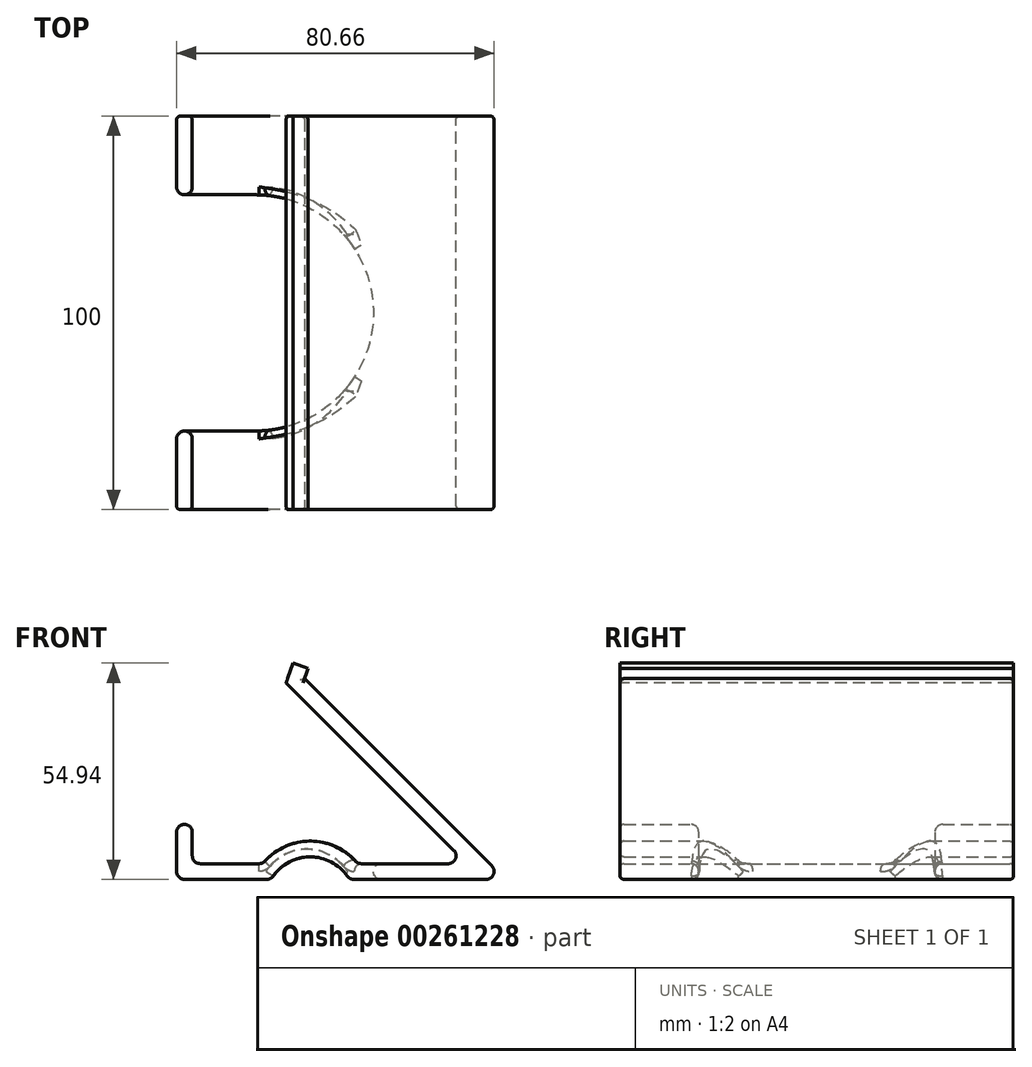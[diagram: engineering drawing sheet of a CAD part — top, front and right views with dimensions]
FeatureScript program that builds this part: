
annotation { "Feature Type Name" : "Feature", "Feature Type Description" : "" }
export const myFeature = defineFeature(function(context is Context, id is Id, definition is map)
    precondition{}
    {
        {
            var Q0;
            Q0=qCreatedBy(makeId("Front.planeOp"),FACE);
            var sketch = newSketch(context, id + "F0", { "sketchPlane" : qUnion([Q0])});
            skLineSegment(sketch, "E0", {"start": v(-39.92, 0) * mm, "end": v(-19.92, 0) * mm});
            skLineSegment(sketch, "E1", {"start": v(-39.92, 4) * mm, "end": v(-39.92, 10) * mm});
            skLineSegment(sketch, "E2", {"start": v(0, 0) * mm, "end": v(0.08, 0) * mm});
            skArc(sketch, "E3", {"start": v(0, 0) * mm, "mid": v(-9.96, 5.74) * mm, "end": v(-19.92, 0) * mm});
            skLineSegment(sketch, "E4.trimOffspring", {"start": v(0, 0) * mm, "end": v(39.57, 0) * mm});
            skLineSegment(sketch, "E5", {"start": v(-0.18, 39.75) * mm, "end": v(39.57, 0) * mm});
            skLineSegment(sketch, "E6.0", {"start": v(2.09, 4) * mm, "end": v(29.91, 4) * mm});
            skLineSegment(sketch, "E6.1", {"start": v(-3, 36.92) * mm, "end": v(29.91, 4) * mm});
            skArc(sketch, "E7.0", {"start": v(2.09, 4) * mm, "mid": v(-9.96, 9.74) * mm, "end": v(-22.01, 4) * mm});
            skLineSegment(sketch, "E8.0", {"start": v(-39.92, 4) * mm, "end": v(-22.01, 4) * mm});
            skLineSegment(sketch, "E9.0", {"start": v(-43.92, 0) * mm, "end": v(-43.92, 10) * mm});
            skLineSegment(sketch, "E10", {"start": v(-39.92, 4) * mm, "end": v(-39.92, 14) * mm});
            skLineSegment(sketch, "E11", {"start": v(-39.92, 14) * mm, "end": v(-43.92, 14) * mm});
            skLineSegment(sketch, "E12", {"start": v(-43.92, 14) * mm, "end": v(-43.92, 10) * mm});
            skLineSegment(sketch, "E13", {"start": v(-43.92, 0) * mm, "end": v(-39.92, 0) * mm});
            skLineSegment(sketch, "E14", {"start": v(-0.18, 39.75) * mm, "end": v(-3, 36.92) * mm});
            skSolve(sketch);
        }
        {
            var Q0;
            Q0 = qSketchRegion(id + "F0", true);
            extrude(context, id + "F1", {"entities" : qUnion([Q0]), "depth" : 100 * mm});
        }
        {
            var Q0;
            Q0=makeQuery(id+"F1.opExtrude","SWEPT_FACE",FACE,{"disambiguationData":[OSD([sQuery(id+"F0.wireOp",EDGE,"E14")])]});
            extrude(context, id + "F2", {"entities" : qUnion([Q0]), "operationType" : NewBodyOperationType.ADD, "depth" : 19.5 * mm});
        }
        {
            var Q0;
            {var subQ0=sQuery(id+"F0.wireOp",EDGE,"E14");Q0=makeQuery(id+"F2.boolean.opBoolean","MERGE",FACE,{"derivedFrom":[makeQuery(id+"F1.opExtrude","CAP_FACE",FACE,{"disambiguationData":[OSD([sQuery(id+"F0.wireOp",EDGE,"E0"),sQuery(id+"F0.wireOp",EDGE,"E3"),sQuery(id+"F0.wireOp",EDGE,"E4.trimOffspring"),sQuery(id+"F0.wireOp",EDGE,"E5"),sQuery(id+"F0.wireOp",EDGE,"E6.0"),sQuery(id+"F0.wireOp",EDGE,"E6.1"),sQuery(id+"F0.wireOp",EDGE,"E7.0"),sQuery(id+"F0.wireOp",EDGE,"E8.0"),sQuery(id+"F0.wireOp",EDGE,"E9.0"),sQuery(id+"F0.wireOp",EDGE,"E10"),sQuery(id+"F0.wireOp",EDGE,"E11"),sQuery(id+"F0.wireOp",EDGE,"E12"),sQuery(id+"F0.wireOp",EDGE,"E13"),subQ0])],"isStart":false}),makeQuery(id+"F2.opExtrude","SWEPT_FACE",FACE,{"disambiguationData":[OSD([subQ0]),TDD([makeQuery(id+"F1.opExtrude","CAP_EDGE",EDGE,{"disambiguationData":[OSD([subQ0])],"isStart":false})])]})]});}
            var sketch = newSketch(context, id + "F3", { "sketchPlane" : qUnion([Q0])});
            skLineSegment(sketch, "E15.0.1", {"start": v(-39.92, 4) * mm, "end": v(-39.92, 14) * mm});
            skLineSegment(sketch, "E15.0.2", {"start": v(-39.92, 14) * mm, "end": v(-43.92, 14) * mm});
            skLineSegment(sketch, "E15.0.3", {"start": v(-43.92, 14) * mm, "end": v(-43.92, 0) * mm});
            skArc(sketch, "E15.0.5", {"start": v(-19.92, 0) * mm, "mid": v(-9.96, 5.74) * mm, "end": v(0, 0) * mm});
            skLineSegment(sketch, "E15.0.6", {"start": v(0, 0) * mm, "end": v(39.57, 0) * mm});
            skArc(sketch, "E15.0.11", {"start": v(2.09, 4) * mm, "mid": v(-9.96, 9.74) * mm, "end": v(-22.01, 4) * mm});
            skLineSegment(sketch, "E16.0", {"start": v(-13.97, 53.54) * mm, "end": v(-16.8, 50.7) * mm});
            skLineSegment(sketch, "E17.0", {"start": v(-13.97, 53.54) * mm, "end": v(-12.16, 51.73) * mm});
            skLineSegment(sketch, "E18", {"start": v(-15.24, 52.26) * mm, "end": v(19.9, 148.83) * mm});
            skLineSegment(sketch, "E19.0", {"start": v(-11.44, 51.01) * mm, "end": v(23.66, 147.46) * mm});
            skLineSegment(sketch, "E20.0", {"start": v(-13.97, 53.54) * mm, "end": v(39.57, 0) * mm});
            skLineSegment(sketch, "E21", {"start": v(19.9, 148.83) * mm, "end": v(23.66, 147.46) * mm});
            skSolve(sketch);
        }
        {
            var Q0;
            Q0 = qSketchRegion(id + "F3", true);
            extrude(context, id + "F4", {"entities" : qUnion([Q0]), "operationType" : NewBodyOperationType.ADD, "oppositeDirection" : true, "depth" : 100 * mm});
        }
        {
            var Q0;
            {var subQ0=sQuery(id+"F0.wireOp",EDGE,"E14");Q0=makeQuery(id+"F4.boolean.opBoolean","MERGE",FACE,{"derivedFrom":[makeQuery(id+"F2.boolean.opBoolean","MERGE",FACE,{"derivedFrom":[makeQuery(id+"F1.opExtrude","CAP_FACE",FACE,{"disambiguationData":[OSD([sQuery(id+"F0.wireOp",EDGE,"E0"),sQuery(id+"F0.wireOp",EDGE,"E3"),sQuery(id+"F0.wireOp",EDGE,"E4.trimOffspring"),sQuery(id+"F0.wireOp",EDGE,"E5"),sQuery(id+"F0.wireOp",EDGE,"E6.0"),sQuery(id+"F0.wireOp",EDGE,"E6.1"),sQuery(id+"F0.wireOp",EDGE,"E7.0"),sQuery(id+"F0.wireOp",EDGE,"E8.0"),sQuery(id+"F0.wireOp",EDGE,"E9.0"),sQuery(id+"F0.wireOp",EDGE,"E10"),sQuery(id+"F0.wireOp",EDGE,"E11"),sQuery(id+"F0.wireOp",EDGE,"E12"),sQuery(id+"F0.wireOp",EDGE,"E13"),subQ0])],"isStart":false}),makeQuery(id+"F2.opExtrude","SWEPT_FACE",FACE,{"disambiguationData":[OSD([subQ0]),TDD([makeQuery(id+"F1.opExtrude","CAP_EDGE",EDGE,{"disambiguationData":[OSD([subQ0])],"isStart":false})])]})]}),makeQuery(id+"F4.opExtrude","CAP_FACE",FACE,{"disambiguationData":[OSD([sQuery(id+"F3.wireOp",EDGE,"E16.0"),sQuery(id+"F3.wireOp",EDGE,"E18"),sQuery(id+"F3.wireOp",EDGE,"E19.0"),sQuery(id+"F3.wireOp",EDGE,"E20.0"),sQuery(id+"F3.wireOp",EDGE,"E21")])],"isStart":true})]});}
            var sketch = newSketch(context, id + "F5", { "sketchPlane" : qUnion([Q0])});
            skLineSegment(sketch, "E22.0", {"start": v(-16.8, 50.7) * mm, "end": v(-16.07, 49.98) * mm});
            skLineSegment(sketch, "E23", {"start": v(-15.24, 52.26) * mm, "end": v(-16.07, 49.98) * mm});
            skLineSegment(sketch, "E24", {"start": v(-15.24, 52.26) * mm, "end": v(-16.8, 50.7) * mm});
            skPoint(sketch, "E25.orphan", {"position": v(29.91, 4) * mm});
            skPoint(sketch, "E26.0.end.orphan", {"position": v(19.9, 148.83) * mm});
            skSolve(sketch);
        }
        {
            var Q0;
            Q0=makeQuery(id+"F5.imprint","IMPRINT",FACE,{"disambiguationData":[TD([[makeQuery(id+"F5.imprint","IMPRINT",EDGE,{"derivedFrom":sQuery(id+"F5.wireOp",EDGE,"E22.0")}),1.0]])]});
            extrude(context, id + "F6", {"entities" : qUnion([Q0]), "operationType" : NewBodyOperationType.REMOVE, "oppositeDirection" : true, "depth" : 108.1 * mm});
        }
        {
            var Q0;
            Q0=makeQuery(id+"F1.opExtrude","SWEPT_EDGE",EDGE,{"disambiguationData":[OSD([sQuery(id+"F0.wireOp",EDGE,"E8.0"),sQuery(id+"F0.wireOp",EDGE,"E10")])]});
            var Q1;
            Q1=makeQuery(id+"F6.boolean.opBoolean","COPY",EDGE,{"derivedFrom":makeQuery(id+"F6.opExtrude","SWEPT_EDGE",EDGE,{"disambiguationData":[OSD([sQuery(id+"F0.wireOp",EDGE,"E6.1"),sQuery(id+"F0.wireOp",EDGE,"E14"),sQuery(id+"F5.wireOp",EDGE,"E22.0"),sQuery(id+"F5.wireOp",EDGE,"E23")])]})});
            var Q2;
            Q2=makeQuery(id+"F4.opExtrude","SWEPT_EDGE",EDGE,{"disambiguationData":[OSD([sQuery(id+"F3.wireOp",EDGE,"E19.0"),sQuery(id+"F3.wireOp",EDGE,"E20.0")])]});
            var Q3;
            Q3=makeQuery(id+"F1.opExtrude","SWEPT_EDGE",EDGE,{"disambiguationData":[OSD([sQuery(id+"F0.wireOp",EDGE,"E4.trimOffspring"),sQuery(id+"F0.wireOp",EDGE,"E5")])]});
            var Q4;
            Q4=makeQuery(id+"F1.opExtrude","SWEPT_EDGE",EDGE,{"disambiguationData":[OSD([sQuery(id+"F0.wireOp",EDGE,"E6.0"),sQuery(id+"F0.wireOp",EDGE,"E6.1")])]});
            var Q5;
            Q5=makeQuery(id+"F1.opExtrude","SWEPT_EDGE",EDGE,{"disambiguationData":[OSD([sQuery(id+"F0.wireOp",EDGE,"E9.0"),sQuery(id+"F0.wireOp",EDGE,"E13")])]});
            var Q6;
            Q6=makeQuery(id+"F1.opExtrude","SWEPT_EDGE",EDGE,{"disambiguationData":[OSD([sQuery(id+"F0.wireOp",EDGE,"E0"),sQuery(id+"F0.wireOp",EDGE,"E3")])]});
            var Q7;
            Q7=makeQuery(id+"F1.opExtrude","SWEPT_EDGE",EDGE,{"disambiguationData":[OSD([sQuery(id+"F0.wireOp",EDGE,"E3"),sQuery(id+"F0.wireOp",EDGE,"E4.trimOffspring")])]});
            var Q8;
            Q8=makeQuery(id+"F1.opExtrude","SWEPT_EDGE",EDGE,{"disambiguationData":[OSD([sQuery(id+"F0.wireOp",EDGE,"E7.0"),sQuery(id+"F0.wireOp",EDGE,"E8.0")])]});
            var Q9;
            Q9=makeQuery(id+"F1.opExtrude","SWEPT_EDGE",EDGE,{"disambiguationData":[OSD([sQuery(id+"F0.wireOp",EDGE,"E6.0"),sQuery(id+"F0.wireOp",EDGE,"E7.0")])]});
            var Q10;
            Q10=makeQuery(id+"F1.opExtrude","SWEPT_EDGE",EDGE,{"disambiguationData":[OSD([sQuery(id+"F0.wireOp",EDGE,"E11"),sQuery(id+"F0.wireOp",EDGE,"E12")])]});
            fillet(context, id + "F7", {"entities" : qUnion([Q0, Q1, Q2, Q3, Q4, Q5, Q6, Q7, Q8, Q9, Q10]), "radius" : 2 * mm, "tangentPropagation" : true, "allowEdgeOverflow" : false});
        }
        {
            var Q0;
            {var subQ0=sQuery(id+"F0.wireOp",EDGE,"E14");var subQ1=sQuery(id+"F0.wireOp",EDGE,"E6.1");Q0=makeQuery(id+"F2.boolean.opBoolean","MERGE",EDGE,{"derivedFrom":[makeQuery(id+"F1.opExtrude","CAP_EDGE",EDGE,{"disambiguationData":[OSD([subQ1])],"isStart":true}),makeQuery(id+"F2.opExtrude","SWEPT_EDGE",EDGE,{"disambiguationData":[OSD([subQ1,subQ0]),TDD([makeQuery(id+"F1.opExtrude","CAP_VERTEX",VERTEX,{"disambiguationData":[OSD([subQ1,subQ0])],"isStart":true})])]})]});}
            var Q1;
            Q1=makeQuery(id+"F6.boolean.opBoolean","MERGE",EDGE,{"derivedFrom":[makeQuery(id+"F4.opExtrude","CAP_EDGE",EDGE,{"disambiguationData":[OSD([sQuery(id+"F3.wireOp",EDGE,"E18")])],"isStart":true}),makeQuery(id+"F6.opExtrude","CAP_EDGE",EDGE,{"disambiguationData":[OSD([sQuery(id+"F5.wireOp",EDGE,"E23")])],"isStart":true})]});
            var Q2;
            {var subQ0=sQuery(id+"F0.wireOp",EDGE,"E14");var subQ1=sQuery(id+"F0.wireOp",EDGE,"E5");Q2=makeQuery(id+"F2.boolean.opBoolean","MERGE",EDGE,{"derivedFrom":[makeQuery(id+"F1.opExtrude","CAP_EDGE",EDGE,{"disambiguationData":[OSD([subQ1])],"isStart":false}),makeQuery(id+"F2.opExtrude","SWEPT_EDGE",EDGE,{"disambiguationData":[OSD([subQ1,subQ0]),TDD([makeQuery(id+"F1.opExtrude","CAP_VERTEX",VERTEX,{"disambiguationData":[OSD([subQ1,subQ0])],"isStart":false})])]})]});}
            var Q3;
            Q3=makeQuery(id+"F4.opExtrude","CAP_EDGE",EDGE,{"disambiguationData":[OSD([sQuery(id+"F3.wireOp",EDGE,"E19.0")])],"isStart":false});
            fillet(context, id + "F8", {"entities" : qUnion([Q0, Q1, Q2, Q3]), "radius" : 1 * mm, "tangentPropagation" : true, "allowEdgeOverflow" : false});
        }
        {
            var Q0;
            Q0=makeQuery(id+"F1.opExtrude","SWEPT_FACE",FACE,{"disambiguationData":[OSD([sQuery(id+"F0.wireOp",EDGE,"E4.trimOffspring")])]});
            cPlane(context, id + "F9", {"entities" : qUnion([Q0]), "cplaneType" : CPlaneType.OFFSET, "offset" : 25 * mm, "width" : 150 * mm, "height" : 150 * mm});
        }
        {
            var Q0;
            Q0=qCreatedBy(id+"F9.planeOp",FACE);
            var sketch = newSketch(context, id + "F10", { "sketchPlane" : qUnion([Q0])});
            skLineSegment(sketch, "E27.0", {"start": v(-43.92, 1) * mm, "end": v(-43.92, 99) * mm});
            skLineSegment(sketch, "E28", {"start": v(-43.92, 50) * mm, "end": v(-43.92, 80) * mm});
            skLineSegment(sketch, "E29", {"start": v(-43.92, 80) * mm, "end": v(-43.92, 20) * mm});
            skLineSegment(sketch, "E30", {"start": v(-43.92, 20) * mm, "end": v(-23.92, 20) * mm});
            skLineSegment(sketch, "E31", {"start": v(-43.92, 80) * mm, "end": v(-23.92, 80) * mm});
            skArc(sketch, "E32", {"start": v(-23.92, 20) * mm, "mid": v(6.08, 50) * mm, "end": v(-23.92, 80) * mm});
            skSolve(sketch);
        }
        {
            var Q0;
            Q0 = qSketchRegion(id + "F10", true);
            extrude(context, id + "F11", {"entities" : qUnion([Q0]), "operationType" : NewBodyOperationType.REMOVE, "oppositeDirection" : true, "depth" : 40.1 * mm});
        }
        {
            var Q0;
            Q0=makeQuery(id+"F11.boolean.opBoolean","INTERSECT",EDGE,{"disambiguationData":[OD(0.0)],"derivedFrom":[makeQuery(id+"F1.opExtrude","SWEPT_FACE",FACE,{"disambiguationData":[OSD([sQuery(id+"F0.wireOp",EDGE,"E7.0")])]}),makeQuery(id+"F11.opExtrude","SWEPT_FACE",FACE,{"disambiguationData":[OSD([sQuery(id+"F10.wireOp",EDGE,"E32")])]})]});
            var Q1;
            Q1=makeQuery(id+"F11.boolean.opBoolean","COPY",EDGE,{"derivedFrom":makeQuery(id+"F11.opExtrude","SWEPT_EDGE",EDGE,{"disambiguationData":[OSD([sQuery(id+"F10.wireOp",EDGE,"E29"),sQuery(id+"F10.wireOp",EDGE,"E30")])]})});
            fillet(context, id + "F12", {"entities" : qUnion([Q0, Q1]), "radius" : 2 * mm, "tangentPropagation" : true, "allowEdgeOverflow" : false});
        }
        {
            var Q0;
            {var subQ0=sQuery(id+"F0.wireOp",EDGE,"E14");Q0=makeQuery(id+"F4.boolean.opBoolean","MERGE",FACE,{"derivedFrom":[makeQuery(id+"F2.boolean.opBoolean","MERGE",FACE,{"derivedFrom":[makeQuery(id+"F1.opExtrude","CAP_FACE",FACE,{"disambiguationData":[OSD([sQuery(id+"F0.wireOp",EDGE,"E0"),sQuery(id+"F0.wireOp",EDGE,"E3"),sQuery(id+"F0.wireOp",EDGE,"E4.trimOffspring"),sQuery(id+"F0.wireOp",EDGE,"E5"),sQuery(id+"F0.wireOp",EDGE,"E6.0"),sQuery(id+"F0.wireOp",EDGE,"E6.1"),sQuery(id+"F0.wireOp",EDGE,"E7.0"),sQuery(id+"F0.wireOp",EDGE,"E8.0"),sQuery(id+"F0.wireOp",EDGE,"E9.0"),sQuery(id+"F0.wireOp",EDGE,"E10"),sQuery(id+"F0.wireOp",EDGE,"E11"),sQuery(id+"F0.wireOp",EDGE,"E12"),sQuery(id+"F0.wireOp",EDGE,"E13"),subQ0])],"isStart":false}),makeQuery(id+"F2.opExtrude","SWEPT_FACE",FACE,{"disambiguationData":[OSD([subQ0]),TDD([makeQuery(id+"F1.opExtrude","CAP_EDGE",EDGE,{"disambiguationData":[OSD([subQ0])],"isStart":false})])]})]}),makeQuery(id+"F4.opExtrude","CAP_FACE",FACE,{"disambiguationData":[OSD([sQuery(id+"F3.wireOp",EDGE,"E16.0"),sQuery(id+"F3.wireOp",EDGE,"E18"),sQuery(id+"F3.wireOp",EDGE,"E19.0"),sQuery(id+"F3.wireOp",EDGE,"E20.0"),sQuery(id+"F3.wireOp",EDGE,"E21")])],"isStart":true})]});}
            var sketch = newSketch(context, id + "F13", { "sketchPlane" : qUnion([Q0])});
            skLineSegment(sketch, "E33.0", {"start": v(-15.63, 51.18) * mm, "end": v(19.9, 148.83) * mm});
            skLineSegment(sketch, "E34.0", {"start": v(23.66, 147.46) * mm, "end": v(-10.71, 53) * mm});
            skPoint(sketch, "E35.orphan", {"position": v(-11, 52.2) * mm});
            skLineSegment(sketch, "E36", {"start": v(23.66, 147.46) * mm, "end": v(19.9, 148.83) * mm});
            skLineSegment(sketch, "E37", {"start": v(-14.27, 54.94) * mm, "end": v(-10.5, 53.57) * mm});
            skSolve(sketch);
        }
        {
            var Q0;
            Q0 = qSketchRegion(id + "F13", true);
            extrude(context, id + "F14", {"entities" : qUnion([Q0]), "operationType" : NewBodyOperationType.REMOVE, "oppositeDirection" : true, "depth" : 116.1 * mm});
        }
    });
